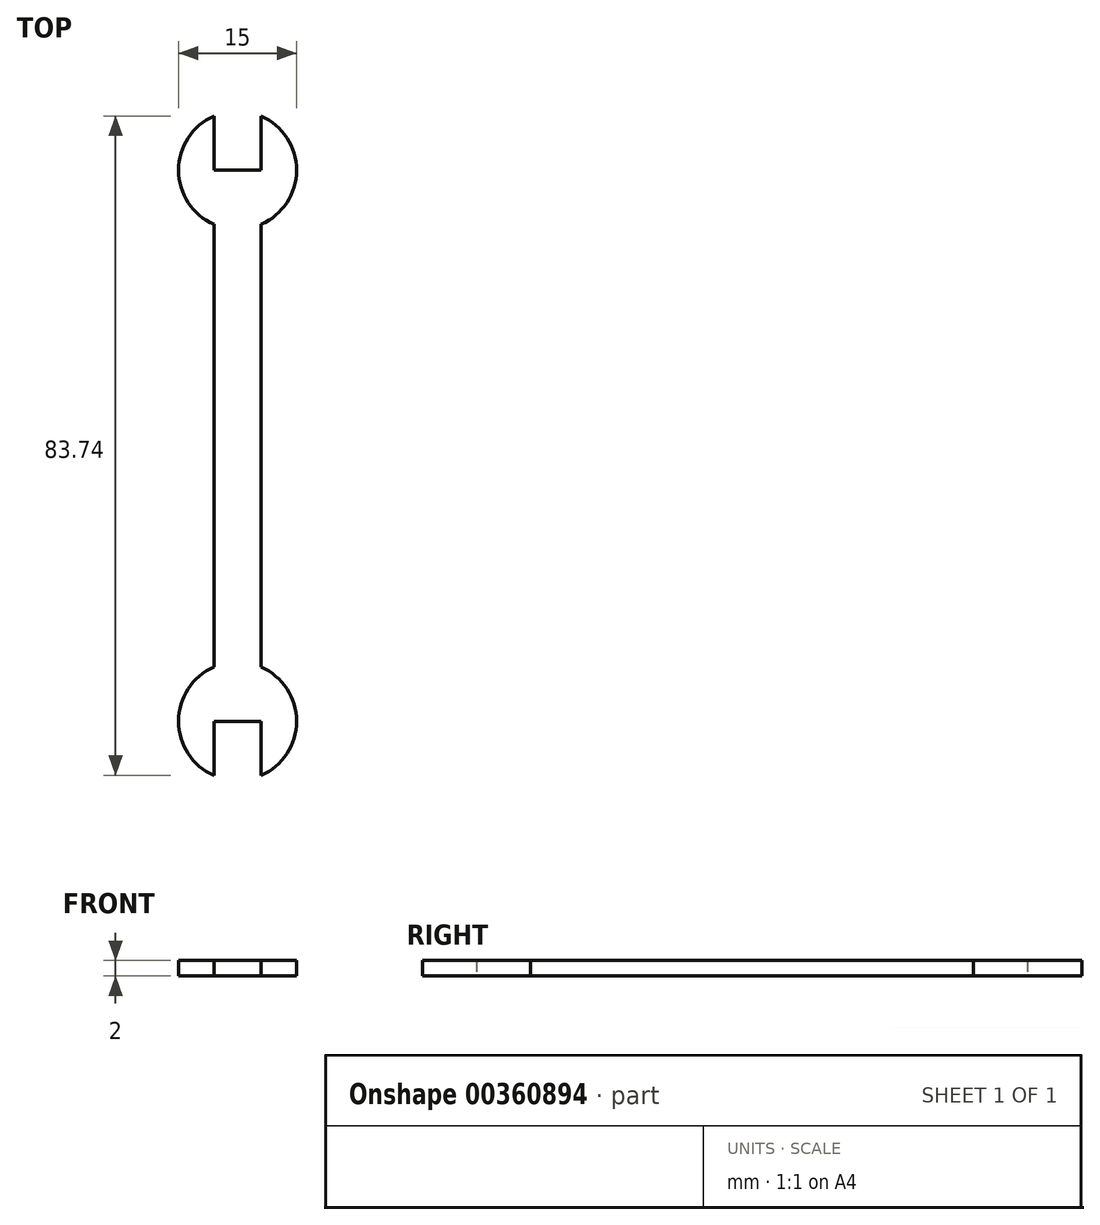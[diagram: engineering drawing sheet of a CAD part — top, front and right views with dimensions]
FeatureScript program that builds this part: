
annotation { "Feature Type Name" : "Feature", "Feature Type Description" : "" }
export const myFeature = defineFeature(function(context is Context, id is Id, definition is map)
    precondition{}
    {
        {
            var Q0;
            Q0=qCreatedBy(makeId("Top.planeOp"),FACE);
            var sketch = newSketch(context, id + "F0", { "sketchPlane" : qUnion([Q0])});
            skLineSegment(sketch, "E0", {"start": v(3, 0) * mm, "end": v(3, 28.13) * mm});
            skArc(sketch, "E1", {"start": v(-3, 41.87) * mm, "mid": v(-7.5, 35) * mm, "end": v(-3, 28.13) * mm});
            skLineSegment(sketch, "E2.MirrorCS", {"start": v(-3, 0) * mm, "end": v(-3, 28.13) * mm});
            skPoint(sketch, "E3.orphan", {"position": v(3, 35) * mm});
            skPoint(sketch, "E4.orphan", {"position": v(-3, 35) * mm});
            skLineSegment(sketch, "E5", {"start": v(-3, 35) * mm, "end": v(3, 35) * mm});
            skArc(sketch, "E6.trimOffspring", {"start": v(3, 28.13) * mm, "mid": v(7.5, 35) * mm, "end": v(3, 41.87) * mm});
            skLineSegment(sketch, "E7.MirrorCS", {"start": v(-3, 0) * mm, "end": v(-3, -28.13) * mm});
            skLineSegment(sketch, "E8.MirrorCS", {"start": v(3, 0) * mm, "end": v(3, -28.13) * mm});
            skArc(sketch, "E9.MirrorCS", {"start": v(3, -28.13) * mm, "mid": v(7.5, -35) * mm, "end": v(3, -41.87) * mm});
            skArc(sketch, "E10.MirrorCS", {"start": v(-3, -41.87) * mm, "mid": v(-7.5, -35) * mm, "end": v(-3, -28.13) * mm});
            skLineSegment(sketch, "E11.MirrorCS", {"start": v(-3, -35) * mm, "end": v(3, -35) * mm});
            skLineSegment(sketch, "E12.trimOffspring", {"start": v(3, 35) * mm, "end": v(3, 41.87) * mm});
            skLineSegment(sketch, "E13.trimOffspring", {"start": v(-3, 35) * mm, "end": v(-3, 41.87) * mm});
            skLineSegment(sketch, "E14.trimOffspring", {"start": v(3, -35) * mm, "end": v(3, -41.87) * mm});
            skLineSegment(sketch, "E15.trimOffspring", {"start": v(-3, -35) * mm, "end": v(-3, -41.87) * mm});
            skSolve(sketch);
        }
        {
            var Q0;
            Q0=makeQuery(id+"F0.imprint","IMPRINT",FACE,{"disambiguationData":[TD([[makeQuery(id+"F0.imprint","IMPRINT",EDGE,{"derivedFrom":sQuery(id+"F0.wireOp",EDGE,"E0")}),1.0]])]});
            extrude(context, id + "F1", {"entities" : qUnion([Q0]), "depth" : 2 * mm, "offsetDistance" : 25 * mm});
        }
    });
